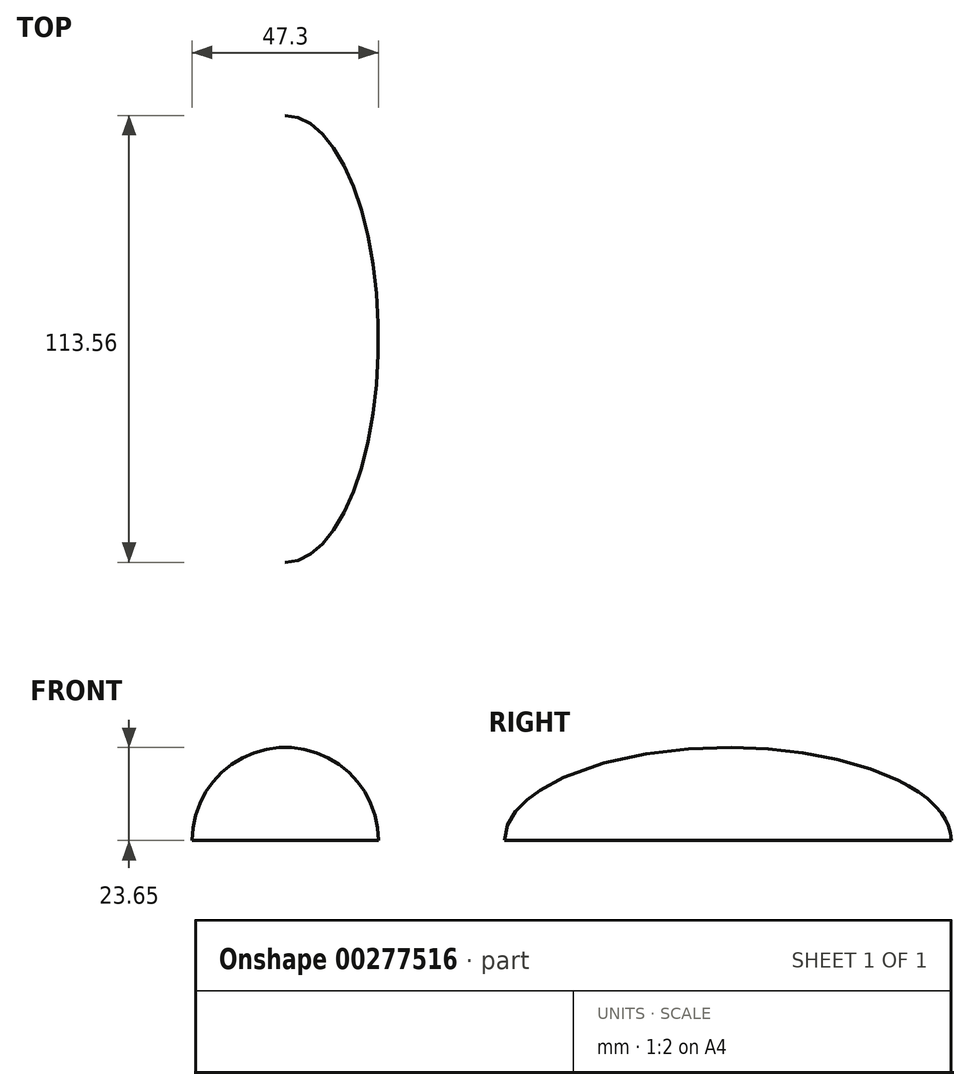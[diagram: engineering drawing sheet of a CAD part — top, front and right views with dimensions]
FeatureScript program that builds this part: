
annotation { "Feature Type Name" : "Feature", "Feature Type Description" : "" }
export const myFeature = defineFeature(function(context is Context, id is Id, definition is map)
    precondition{}
    {
        {
            var Q0;
            Q0=qCreatedBy(makeId("Top.planeOp"),FACE);
            var sketch = newSketch(context, id + "F0", { "sketchPlane" : qUnion([Q0])});
            skEllipse(sketch, "E0", {"center": v(0, 0) * mm, "majorRadius": 56.78 * mm, "minorRadius": 23.65 * mm, "majorAxis": v(0, 1)});
            skLineSegment(sketch, "E1", {"start": v(0, -56.78) * mm, "end": v(0, 56.78) * mm});
            skSolve(sketch);
        }
        {
            var Q0;
            {var subQ0=sQuery(id+"F0.wireOp",EDGE,"E1");Q0=makeQuery(id+"F0.imprint","IMPRINT",FACE,{"disambiguationData":[TD([[makeQuery(id+"F0.imprint","IMPRINT",EDGE,{"derivedFrom":subQ0}),-1.0]])]});}
            var Q1;
            Q1=sQuery(id+"F0.wireOp",EDGE,"E1");
            revolve(context, id + "F1", {"entities" : qUnion([Q0]), "axis" : qUnion([Q1]), "revolveType" : RevolveType.ONE_DIRECTION, "oppositeDirection" : true, "angle" : 180 * degree});
        }
    });
